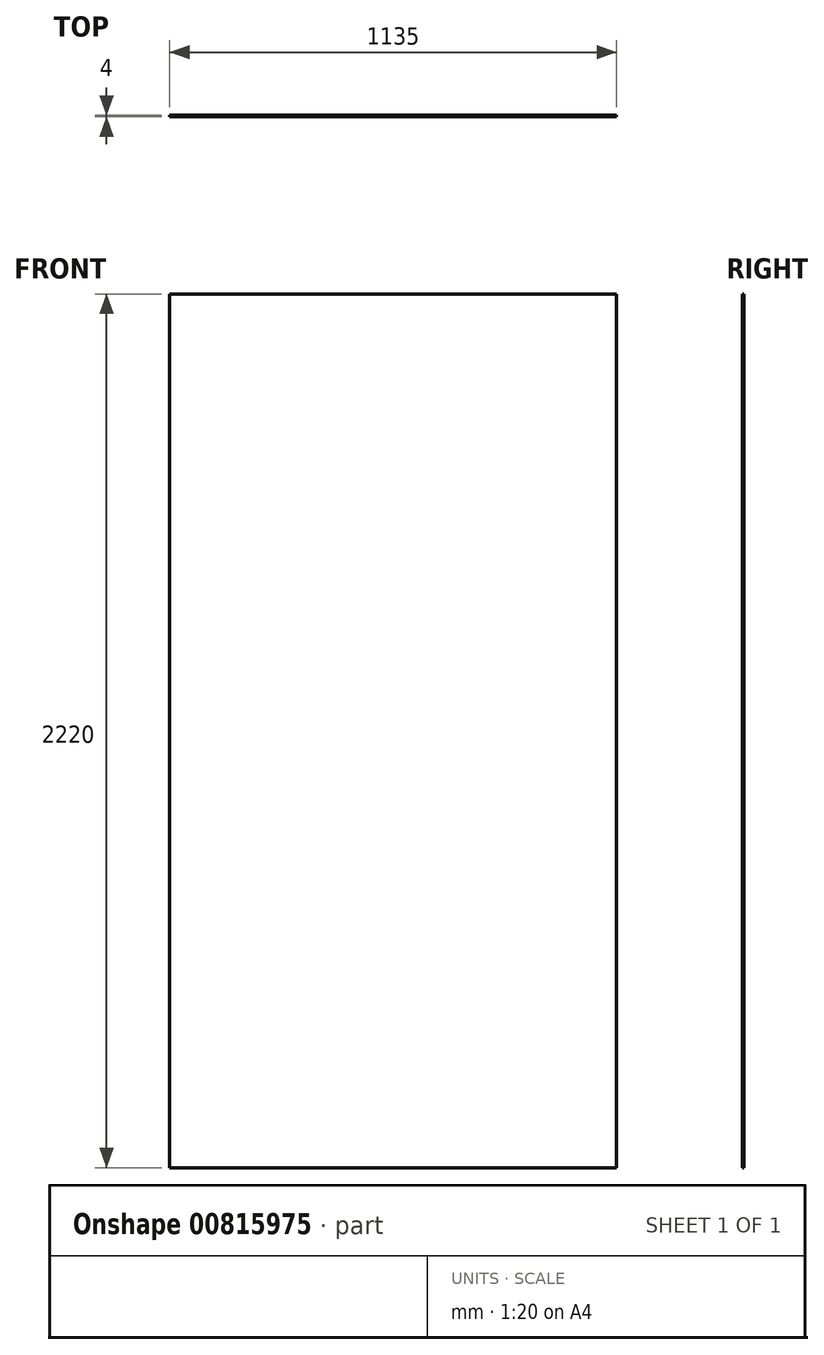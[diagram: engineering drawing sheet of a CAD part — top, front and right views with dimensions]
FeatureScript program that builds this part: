
annotation { "Feature Type Name" : "Feature", "Feature Type Description" : "" }
export const myFeature = defineFeature(function(context is Context, id is Id, definition is map)
    precondition{}
    {
        {
            var Q0;
            Q0=qCreatedBy(makeId("Front.planeOp"),FACE);
            var sketch = newSketch(context, id + "F0", { "sketchPlane" : qUnion([Q0])});
            skLineSegment(sketch, "E0.bottom", {"start": v(0, 0) * mm, "end": v(1135, 0) * mm});
            skLineSegment(sketch, "E0.top", {"start": v(0, 2220) * mm, "end": v(1135, 2220) * mm});
            skLineSegment(sketch, "E0.left", {"start": v(0, 0) * mm, "end": v(0, 2220) * mm});
            skLineSegment(sketch, "E0.right", {"start": v(1135, 0) * mm, "end": v(1135, 2220) * mm});
            skSolve(sketch);
        }
        {
            var Q0;
            Q0 = qSketchRegion(id + "F0", true);
            extrude(context, id + "F1", {"entities" : qUnion([Q0]), "depth" : 4 * mm, "offsetDistance" : 25 * mm});
        }
    });
